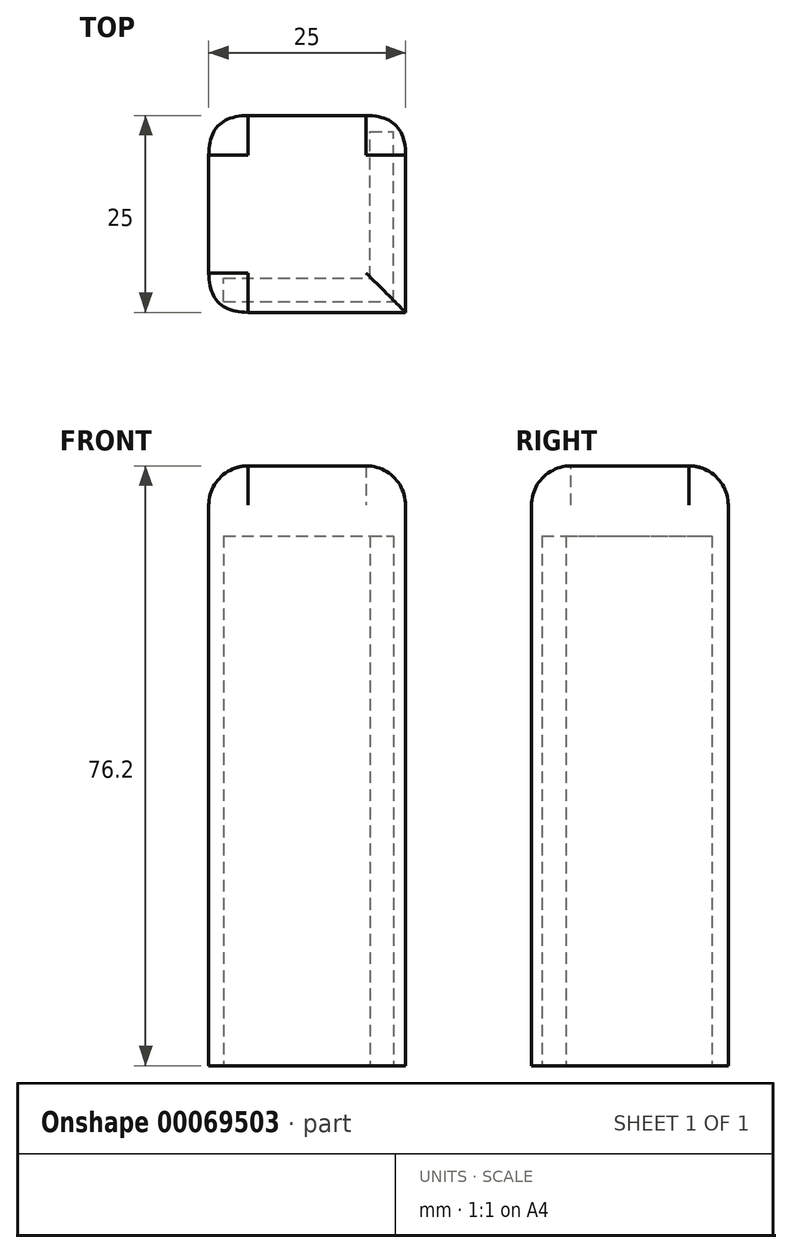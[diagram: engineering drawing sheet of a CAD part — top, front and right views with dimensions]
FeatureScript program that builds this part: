
annotation { "Feature Type Name" : "Feature", "Feature Type Description" : "" }
export const myFeature = defineFeature(function(context is Context, id is Id, definition is map)
    precondition{}
    {
        {
            var Q0;
            Q0=qCreatedBy(makeId("Top.planeOp"),FACE);
            var sketch = newSketch(context, id + "F0", { "sketchPlane" : qUnion([Q0])});
            skLineSegment(sketch, "E0.bottom", {"start": v(-25.18, 5.2) * mm, "end": v(-0.18, 5.2) * mm});
            skLineSegment(sketch, "E0.top", {"start": v(-25.18, -19.8) * mm, "end": v(-0.18, -19.8) * mm});
            skLineSegment(sketch, "E0.left", {"start": v(-25.18, 5.2) * mm, "end": v(-25.18, -19.8) * mm});
            skLineSegment(sketch, "E0.right", {"start": v(-0.18, 5.2) * mm, "end": v(-0.18, -19.8) * mm});
            skSolve(sketch);
        }
        {
            var Q0;
            Q0=makeQuery(id+"F0.imprint","IMPRINT",FACE,{"disambiguationData":[TD([[makeQuery(id+"F0.imprint","IMPRINT",EDGE,{"derivedFrom":sQuery(id+"F0.wireOp",EDGE,"E0.bottom")}),-1.0]])]});
            extrude(context, id + "F1", {"entities" : qUnion([Q0]), "depth" : 76.2 * mm});
        }
        {
            var Q0;
            Q0=makeQuery(id+"F1.opExtrude","CAP_FACE",FACE,{"disambiguationData":[OSD([sQuery(id+"F0.wireOp",EDGE,"E0.bottom"),sQuery(id+"F0.wireOp",EDGE,"E0.top"),sQuery(id+"F0.wireOp",EDGE,"E0.left"),sQuery(id+"F0.wireOp",EDGE,"E0.right")])],"isStart":true});
            var sketch = newSketch(context, id + "F2", { "sketchPlane" : qUnion([Q0])});
            skLineSegment(sketch, "E1.bottom", {"start": v(-23.27, 18.45) * mm, "end": v(-1.68, 18.45) * mm});
            skLineSegment(sketch, "E1.top", {"start": v(-23.27, 15.45) * mm, "end": v(-1.68, 15.45) * mm});
            skLineSegment(sketch, "E1.left", {"start": v(-23.27, 18.45) * mm, "end": v(-23.27, 15.45) * mm});
            skLineSegment(sketch, "E1.right", {"start": v(-1.68, 18.45) * mm, "end": v(-1.68, 15.45) * mm});
            skLineSegment(sketch, "E2.bottom", {"start": v(-4.68, 18.45) * mm, "end": v(-1.68, 18.45) * mm});
            skLineSegment(sketch, "E2.top", {"start": v(-4.68, -3.14) * mm, "end": v(-1.68, -3.14) * mm});
            skLineSegment(sketch, "E2.left", {"start": v(-4.68, 18.45) * mm, "end": v(-4.68, -3.14) * mm});
            skLineSegment(sketch, "E2.right", {"start": v(-1.68, 18.45) * mm, "end": v(-1.68, -3.14) * mm});
            skSolve(sketch);
        }
        {
            var Q0;
            {var subQ0=sQuery(id+"F2.wireOp",EDGE,"E1.bottom");Q0=makeQuery(id+"F2.imprint","IMPRINT",FACE,{"disambiguationData":[TD([[makeQuery(id+"F2.imprint","IMPRINT",EDGE,{"derivedFrom":subQ0}),-1.0]])]});}
            var Q1;
            {var subQ5=sQuery(id+"F2.wireOp",EDGE,"E2.top");Q1=makeQuery(id+"F2.imprint","IMPRINT",FACE,{"disambiguationData":[TD([[makeQuery(id+"F2.imprint","IMPRINT",EDGE,{"derivedFrom":subQ5}),1.0]])]});}
            var Q2;
            {var subQ5=sQuery(id+"F2.wireOp",EDGE,"E2.bottom");Q2=makeQuery(id+"F2.imprint","IMPRINT",FACE,{"disambiguationData":[TD([[makeQuery(id+"F2.imprint","IMPRINT",EDGE,{"derivedFrom":subQ5}),-1.0]])]});}
            extrude(context, id + "F3", {"entities" : qUnion([Q0, Q1, Q2]), "operationType" : NewBodyOperationType.REMOVE, "oppositeDirection" : true, "depth" : 67.3 * mm});
        }
        {
            var Q0;
            Q0=makeQuery(id+"F1.opExtrude","CAP_EDGE",EDGE,{"disambiguationData":[OSD([sQuery(id+"F0.wireOp",EDGE,"E0.top")])],"isStart":false});
            var Q1;
            Q1=makeQuery(id+"F1.opExtrude","CAP_EDGE",EDGE,{"disambiguationData":[OSD([sQuery(id+"F0.wireOp",EDGE,"E0.right")])],"isStart":false});
            var Q2;
            Q2=makeQuery(id+"F1.opExtrude","CAP_EDGE",EDGE,{"disambiguationData":[OSD([sQuery(id+"F0.wireOp",EDGE,"E0.bottom")])],"isStart":false});
            var Q3;
            Q3=makeQuery(id+"F1.opExtrude","CAP_EDGE",EDGE,{"disambiguationData":[OSD([sQuery(id+"F0.wireOp",EDGE,"E0.left")])],"isStart":false});
            fillet(context, id + "F4", {"entities" : qUnion([Q0, Q1, Q2, Q3]), "radius" : 5 * mm, "tangentPropagation" : true, "allowEdgeOverflow" : false});
        }
        {
            var Q0;
            Q0=makeQuery(id+"F1.opExtrude","SWEPT_EDGE",EDGE,{"disambiguationData":[OSD([sQuery(id+"F0.wireOp",EDGE,"E0.bottom"),sQuery(id+"F0.wireOp",EDGE,"E0.left")])]});
            var Q1;
            Q1=makeQuery(id+"F1.opExtrude","SWEPT_EDGE",EDGE,{"disambiguationData":[OSD([sQuery(id+"F0.wireOp",EDGE,"E0.top"),sQuery(id+"F0.wireOp",EDGE,"E0.left")])]});
            var Q2;
            Q2=makeQuery(id+"F1.opExtrude","SWEPT_EDGE",EDGE,{"disambiguationData":[OSD([sQuery(id+"F0.wireOp",EDGE,"E0.bottom"),sQuery(id+"F0.wireOp",EDGE,"E0.right")])]});
            fillet(context, id + "F5", {"entities" : qUnion([Q0, Q1, Q2]), "radius" : 5 * mm, "tangentPropagation" : true, "rho" : 0.5, "crossSection" : FilletCrossSection.CONIC, "allowEdgeOverflow" : false});
        }
    });
